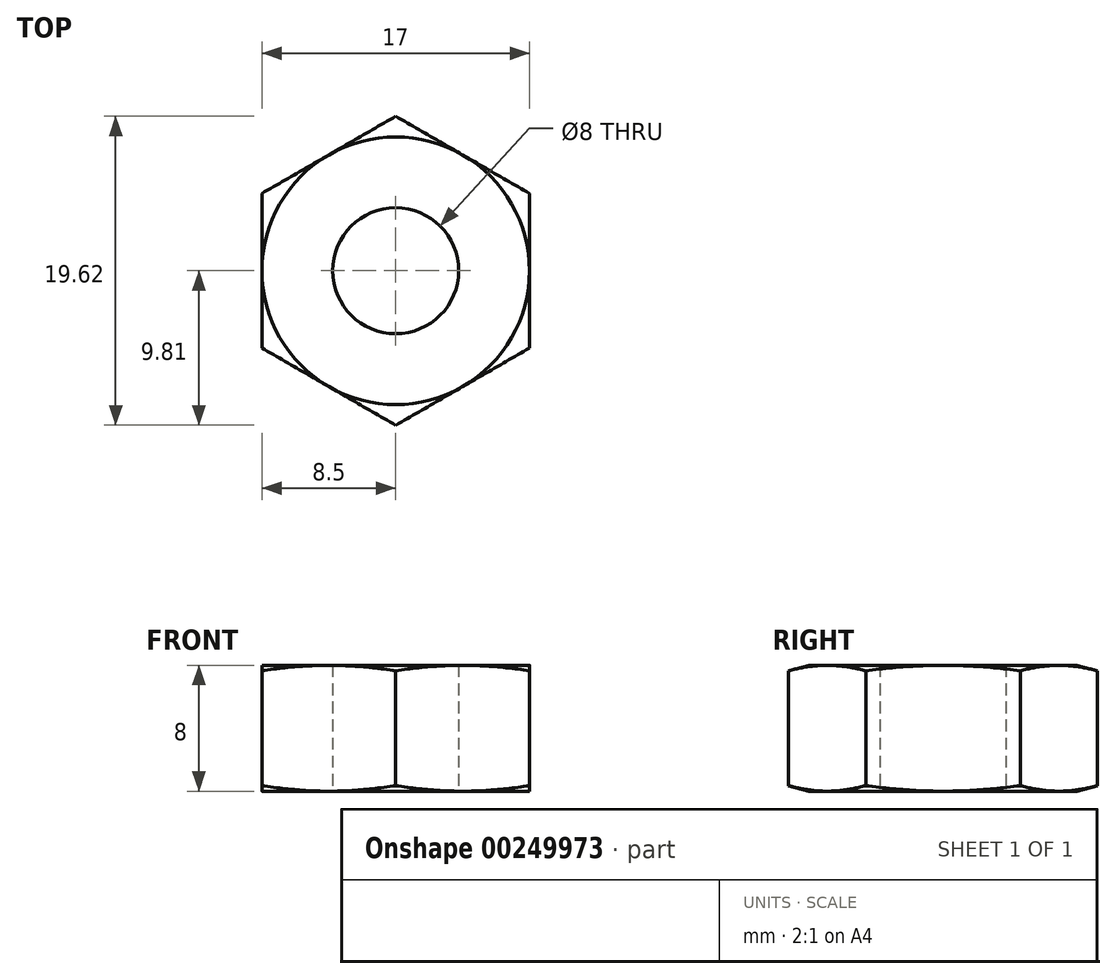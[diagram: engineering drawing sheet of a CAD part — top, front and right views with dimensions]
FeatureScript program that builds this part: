
annotation { "Feature Type Name" : "Feature", "Feature Type Description" : "" }
export const myFeature = defineFeature(function(context is Context, id is Id, definition is map)
    precondition{}
    {
        {
            var Q0;
            Q0=qCreatedBy(makeId("Top.planeOp"),FACE);
            var sketch = newSketch(context, id + "F0", { "sketchPlane" : qUnion([Q0])});
            skCircle(sketch, "E0.cCircle", {"center": v(0, 0) * mm, "radius": 8.5 * mm, "construction": true});
            skLineSegment(sketch, "E0.0", {"start": v(8.5, 4.9) * mm, "end": v(8.5, -4.9) * mm});
            skLineSegment(sketch, "E0.1", {"start": v(8.5, -4.9) * mm, "end": v(0, -9.81) * mm});
            skLineSegment(sketch, "E0.2", {"start": v(0, -9.81) * mm, "end": v(-8.5, -4.9) * mm});
            skLineSegment(sketch, "E0.3", {"start": v(-8.5, -4.9) * mm, "end": v(-8.5, 4.9) * mm});
            skLineSegment(sketch, "E0.4", {"start": v(-8.5, 4.9) * mm, "end": v(0, 9.81) * mm});
            skLineSegment(sketch, "E0.5", {"start": v(0, 9.81) * mm, "end": v(8.5, 4.9) * mm});
            skPoint(sketch, "E0.0.midPoint", {"position": v(8.5, 0) * mm});
            skCircle(sketch, "E1", {"center": v(0, 0) * mm, "radius": 4 * mm});
            skLineSegment(sketch, "E2", {"start": v(-12.53, -7.23) * mm, "end": v(14.01, 8.09) * mm, "construction": true});
            skPoint(sketch, "E3", {"position": v(-7.36, -4.25) * mm});
            skPoint(sketch, "E4", {"position": v(-8.5, -4.9) * mm});
            skSolve(sketch);
        }
        {
            var Q0;
            Q0=qSketchRegion(id+"F0",true);
            extrude(context, id + "F1", {"entities" : qUnion([Q0]), "depth" : 8 * mm});
        }
        {
            var Q0;
            Q0=makeQuery(id+"F1.opExtrude","SWEPT_EDGE",EDGE,{"disambiguationData":[OSD([sQuery(id+"F0.wireOp",EDGE,"E0.2"),sQuery(id+"F0.wireOp",EDGE,"E0.3")])]});
            cPoint(context, id + "F2", {"entities" : qUnion([Q0]), "parameter" : 0.5});
        }
        {
            var Q0;
            Q0=makeQuery(id+"F1.opExtrude","SWEPT_EDGE",EDGE,{"disambiguationData":[OSD([sQuery(id+"F0.wireOp",EDGE,"E0.0"),sQuery(id+"F0.wireOp",EDGE,"E0.5")])]});
            cPoint(context, id + "F3", {"entities" : qUnion([Q0]), "parameter" : 0.5});
        }
        {
            var Q0;
            Q0=qCreatedBy(id+"F2",VERTEX);
            var Q1;
            Q1=qCreatedBy(id+"F3",VERTEX);
            var Q2;
            Q2=makeQuery(id+"F1.opExtrude","CAP_VERTEX",VERTEX,{"disambiguationData":[OSD([sQuery(id+"F0.wireOp",EDGE,"E0.0"),sQuery(id+"F0.wireOp",EDGE,"E0.5")])],"isStart":true});
            cPlane(context, id + "F4", {"entities" : qUnion([Q0, Q1, Q2]), "cplaneType" : CPlaneType.THREE_POINT, "offset" : 25 * mm, "width" : 150 * mm, "height" : 150 * mm});
        }
        {
            var Q0;
            Q0=qCreatedBy(id+"F4.planeOp",FACE);
            var sketch = newSketch(context, id + "F5", { "sketchPlane" : qUnion([Q0])});
            skPoint(sketch, "E5.0", {"position": v(-8.5, 0) * mm});
            skLineSegment(sketch, "E6", {"start": v(-2.9, -1.5) * mm, "end": v(-15.32, 1.83) * mm});
            skPoint(sketch, "E7", {"position": v(-9.81, 8) * mm});
            skPoint(sketch, "E8", {"position": v(-9.81, 4) * mm});
            skLineSegment(sketch, "E9", {"start": v(-13.9, 4) * mm, "end": v(7.47, 4) * mm, "construction": true});
            skLineSegment(sketch, "E10", {"start": v(-15.32, -1.5) * mm, "end": v(-2.9, -1.5) * mm});
            skLineSegment(sketch, "E11", {"start": v(0, -0.96) * mm, "end": v(0, 9.49) * mm, "construction": true});
            skPoint(sketch, "E12.trimOffspring.end.orphan", {"position": v(-9.81, 0) * mm});
            skLineSegment(sketch, "E13", {"start": v(-15.32, 1.83) * mm, "end": v(-15.32, -1.5) * mm});
            skPoint(sketch, "E14.end.orphan", {"position": v(-10.64, -1.5) * mm});
            skPoint(sketch, "E14.start.orphan", {"position": v(-10.64, 0.57) * mm});
            skPoint(sketch, "E15.MirrorCS.start.orphan", {"position": v(-10.64, 7.43) * mm});
            skLineSegment(sketch, "E16.MirrorCS", {"start": v(-15.32, 6.17) * mm, "end": v(-15.32, 9.5) * mm});
            skLineSegment(sketch, "E17.MirrorCS", {"start": v(-2.9, 9.5) * mm, "end": v(-15.32, 6.17) * mm});
            skLineSegment(sketch, "E18.MirrorCS", {"start": v(-15.32, 9.5) * mm, "end": v(-2.9, 9.5) * mm});
            skPoint(sketch, "E19.MirrorP", {"position": v(-8.5, 8) * mm});
            skSolve(sketch);
        }
        {
            var Q0;
            Q0=makeQuery(id+"F5.imprint","IMPRINT",FACE,{"disambiguationData":[TD([[makeQuery(id+"F5.imprint","IMPRINT",EDGE,{"derivedFrom":sQuery(id+"F5.wireOp",EDGE,"E16.MirrorCS")}),-1.0]])]});
            var Q1;
            Q1=makeQuery(id+"F5.imprint","IMPRINT",FACE,{"disambiguationData":[TD([[makeQuery(id+"F5.imprint","IMPRINT",EDGE,{"derivedFrom":sQuery(id+"F5.wireOp",EDGE,"E6")}),1.0]])]});
            var Q2;
            Q2=sQuery(id+"F5.wireOp",EDGE,"E11");
            revolve(context, id + "F6", {"operationType" : NewBodyOperationType.REMOVE, "entities" : qUnion([Q0, Q1]), "axis" : qUnion([Q2]), "revolveType" : RevolveType.FULL, "oppositeDirection" : true});
        }
    });
